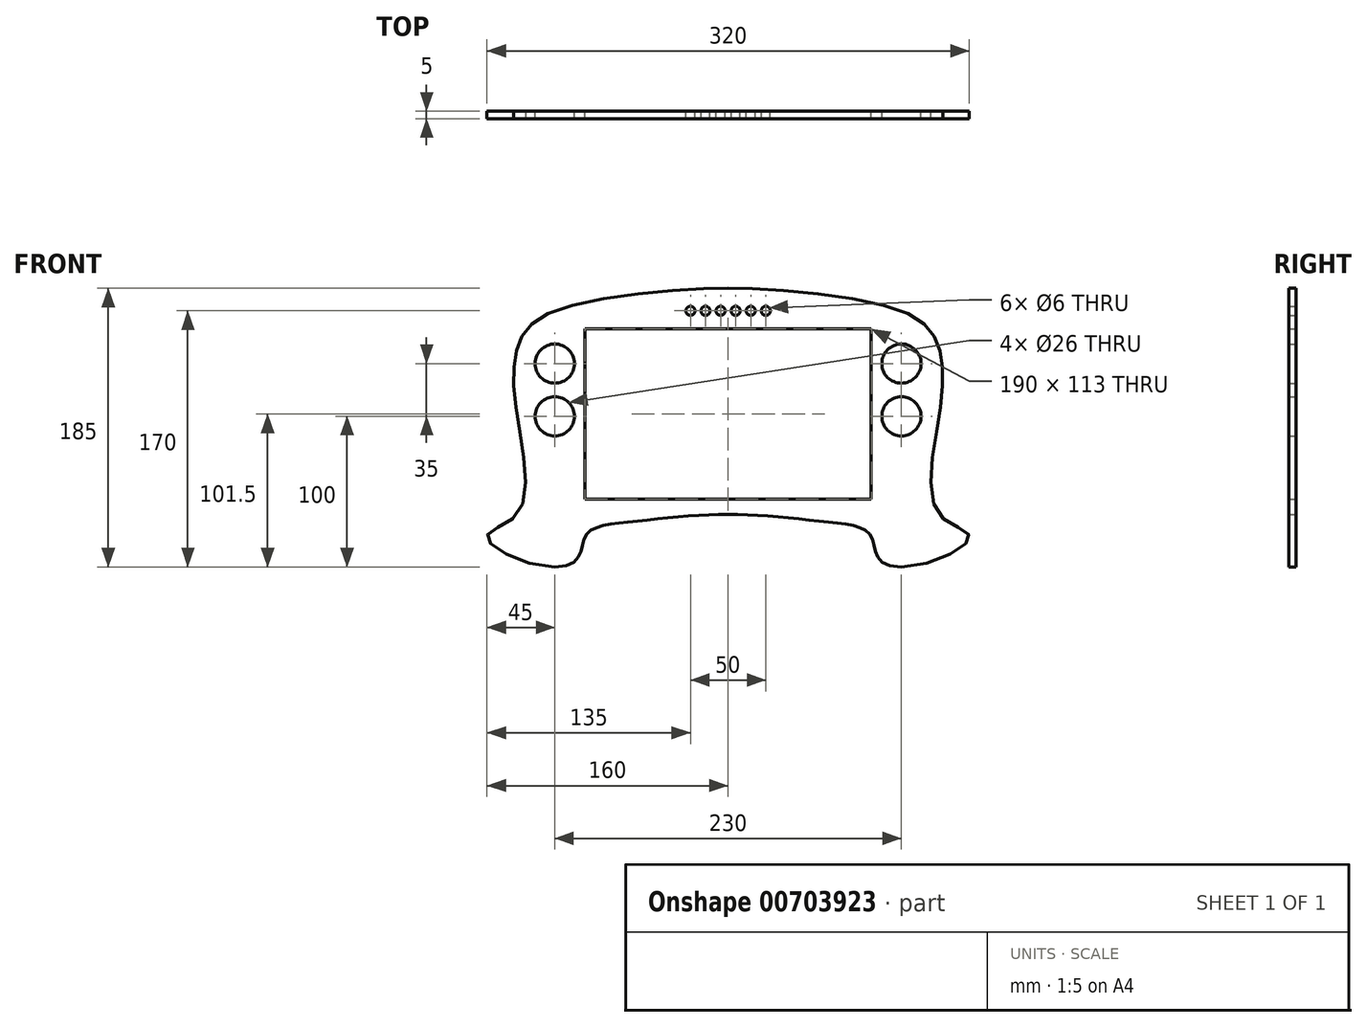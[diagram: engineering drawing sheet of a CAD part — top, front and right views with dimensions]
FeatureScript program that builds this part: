
annotation { "Feature Type Name" : "Feature", "Feature Type Description" : "" }
export const myFeature = defineFeature(function(context is Context, id is Id, definition is map)
    precondition{}
    {
        {
            var Q0;
            Q0=qCreatedBy(makeId("Front.planeOp"),FACE);
            var sketch = newSketch(context, id + "F0", { "sketchPlane" : qUnion([Q0])});
            skLineSegment(sketch, "E0", {"start": v(-84, 52) * mm, "end": v(84, 52) * mm});
            skLineSegment(sketch, "E1", {"start": v(84, 52) * mm, "end": v(84, -52) * mm});
            skLineSegment(sketch, "E2", {"start": v(84, -52) * mm, "end": v(-84, -52) * mm});
            skLineSegment(sketch, "E3", {"start": v(-84, -52) * mm, "end": v(-84, 52) * mm});
            skLineSegment(sketch, "E4", {"start": v(-95, 58) * mm, "end": v(95, 58) * mm});
            skLineSegment(sketch, "E5", {"start": v(95, 58) * mm, "end": v(95, -55) * mm});
            skLineSegment(sketch, "E6", {"start": v(95, -55) * mm, "end": v(-95, -55) * mm});
            skLineSegment(sketch, "E7", {"start": v(-95, -55) * mm, "end": v(-95, 58) * mm});
            skFitSpline(sketch, "E8", {"points": [v(-115, -100) * mm, v(-160, -80) * mm, v(-140, -65) * mm, v(-140, 0) * mm, v(-140, 45) * mm, v(-115, 70) * mm, v(0, 85) * mm], "startDerivative": vector(-371.96, 0) * mm, "endDerivative": vector(302.97, 0) * mm});
            skFitSpline(sketch, "E9", {"points": [v(-115, -100) * mm, v(-95, -80) * mm, v(-65, -70) * mm, v(0, -65) * mm], "startDerivative": vector(214.53, 0) * mm, "endDerivative": vector(141.3, 0) * mm});
            skCircle(sketch, "E10", {"center": v(-115, 35) * mm, "radius": 13 * mm});
            skCircle(sketch, "E11", {"center": v(-115, 0) * mm, "radius": 13 * mm});
            skLineSegment(sketch, "E12", {"start": v(0, 85) * mm, "end": v(0, -65) * mm});
            skFitSpline(sketch, "E13.MirrorCS", {"points": [v(115, -100) * mm, v(160, -80) * mm, v(140, -65) * mm, v(140, 0) * mm, v(140, 45) * mm, v(115, 70) * mm, v(0, 85) * mm], "startDerivative": vector(371.96, 0) * mm, "endDerivative": vector(-302.97, 0) * mm});
            skFitSpline(sketch, "E14.MirrorCS", {"points": [v(115, -100) * mm, v(95, -80) * mm, v(65, -70) * mm, v(0, -65) * mm], "startDerivative": vector(-214.53, 0) * mm, "endDerivative": vector(-141.3, 0) * mm});
            skCircle(sketch, "E15.MirrorC", {"center": v(115, 35) * mm, "radius": 13 * mm});
            skCircle(sketch, "E16.MirrorC", {"center": v(115, 0) * mm, "radius": 13 * mm});
            skCircle(sketch, "E17", {"center": v(-5, 70) * mm, "radius": 3 * mm});
            skCircle(sketch, "E18", {"center": v(-15, 70) * mm, "radius": 3 * mm});
            skCircle(sketch, "E19", {"center": v(-25, 70) * mm, "radius": 3 * mm});
            skCircle(sketch, "E20.MirrorC", {"center": v(5, 70) * mm, "radius": 3 * mm});
            skCircle(sketch, "E21.MirrorC", {"center": v(15, 70) * mm, "radius": 3 * mm});
            skCircle(sketch, "E22.MirrorC", {"center": v(25, 70) * mm, "radius": 3 * mm});
            skSolve(sketch);
        }
        {
            var Q0;
            {var subQ1=sQuery(id+"F0.wireOp",EDGE,"E7");Q0=makeQuery(id+"F0.imprint","IMPRINT",FACE,{"disambiguationData":[TD([[makeQuery(id+"F0.imprint","IMPRINT",EDGE,{"derivedFrom":subQ1}),1.0]])]});}
            var Q1;
            {var subQ5=sQuery(id+"F0.wireOp",EDGE,"E5");Q1=makeQuery(id+"F0.imprint","IMPRINT",FACE,{"disambiguationData":[TD([[makeQuery(id+"F0.imprint","IMPRINT",EDGE,{"derivedFrom":subQ5}),1.0]])]});}
            extrude(context, id + "F1", {"entities" : qUnion([Q0, Q1]), "depth" : 5 * mm, "offsetDistance" : 25 * mm});
        }
    });
